# Revit family: O5MAK-NRG
name_source: partatom
category: Mechanical Equipment
revit_build: Autodesk Revit 2017 (Build: 20181011_1645(x64)
units: mm (PartAtom-declared; Revit-internal decimal feet)

## family parameters
Always vertical = Yes
Cut with Voids When Loaded = No
OmniClass Number = 23.40.40.11.17
OmniClass Title = Refrigerated Cases
Part Type = Normal
Room Calculation Point = No
Round Connector Dimension = Use Radius
Shared = No
Work Plane-Based = Yes

## types (2) — shared parameters
24" Shelf = Yes
BOTTOM ELECTRICAL = Yes
BOTTOM REFRIGERATION PIPING = Yes
Certifications = NSF 7, UL471, CSA
Condensing  Data Volts = 208 V
Condensing Data  Phase = 1
Condensing Frequency (Hz) = 60 Hz
DATE = 05/20/2016
DESIGNERS NAME = SHIDDRAMESH
DRAIN LINE = 36"
DRAIN PIPING = Yes
Default Elevation = 48"
Defrosts Per Day = 6
Description = Multi-Deck Merchandiser
Discharge Air (°F) = 31 °F
Discharge Air Velocity (FPM) = 200 FPM
Drain Pump Amps = 1 A
Drain Pump Watts = 47 W
EQUIPMENT DESCRIPTION = Multi-Deck Merchandiser
EQUIPMENT MARK = O5DMA-NRG
Evaporator Pan Heater  Amps = 7 A
Evaporator Pan Heater  Watts = 1500 W
GLASS = Glass
Height = 101 5/8"
High Efficiency Amps = 0 A
High Efficiency Watts = 28 W
Item Description = Multi-Deck Merchandiser
LF STD END = Yes
Legend Number = O5DMA-NRG
Manufacturer = HILL PHOENIX
Maximum Lights Amps = 0 A
Model = O5DMA-NRG
Number of Fans = 2
PAINTED METAL UPPER SHELF = PAINTED SHELVES
REAR REFRIGERATION PIPING = Yes
RT STD END = Yes
Refrigerant = R404A
Suction Pressure @ Case Outlet (psig) = 58.00 psi
Superheat Set Point @ Bulb (°F) = 6-8  °F
System Data Phase = 1
System Data Volts = 208 V
Systems Frequency = 60 Hz
Systems Wire = 3 wire + ground
TOP ELECTRICAL = Yes
TOP REFRIGERATION PIPING = Yes
Timed-Off Defrost Fail-Safe (Min) = 45 (min)
Timed-Off Defrost Termination Temp = 42 °F
URL = http://www.hillphoenix.com
Width = 43 1/4"

## per-type parameters (varying)
| type | CENTER LINE | CONDENSING UNIT LOCATION | Condensed Horsepower | Lbs. of Refrigerant | Length | Length of Cases | Locked Rotor (LRA) Amps | Maximum Lights Watts | Refgn | Running Load (RLA) Amps | Systems Maximum Overcurrent Protection | Systems Minimum Circuit Amps |
| 4' | 24" | 40" | 1 | 4.5 | 48" | 48" | 46 A | 35 W | 22 1/2" | 10 A | 25 A | 21 A |
| 6' | 36" | 67" | 1 - 3/4 | 5.2 | 72" | 0" | 55 A | 56 W | 28 5/8" | 13 A | 35 A | 25 A |

## geometry (parser evidence)
native form markers: Blend x10, Sweep x3
no freeform markers — native parametric forms only
